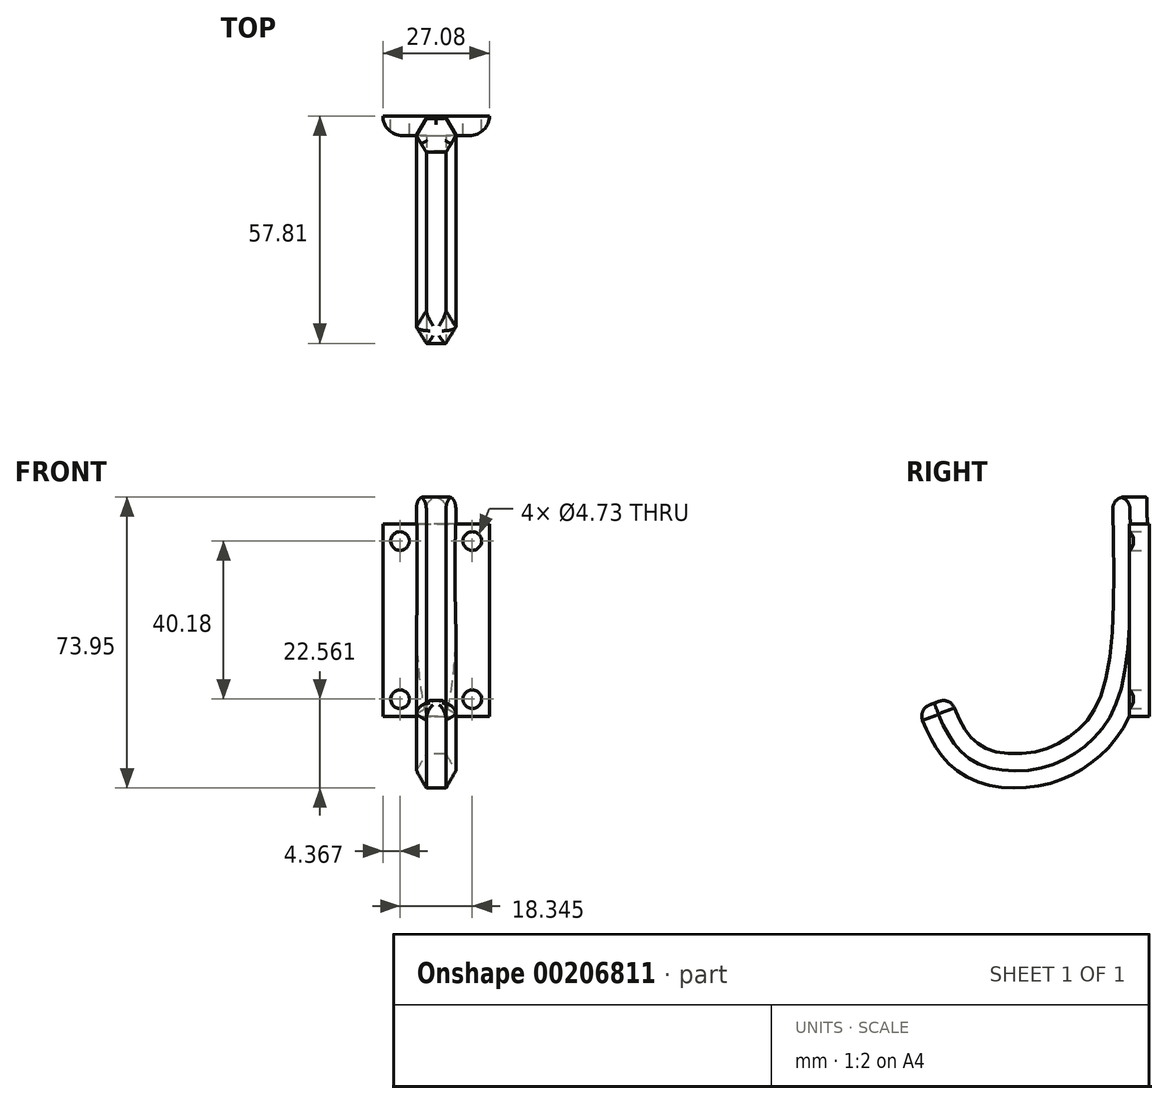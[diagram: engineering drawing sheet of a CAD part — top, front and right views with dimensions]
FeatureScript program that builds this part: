
annotation { "Feature Type Name" : "Feature", "Feature Type Description" : "" }
export const myFeature = defineFeature(function(context is Context, id is Id, definition is map)
    precondition{}
    {
        {
            var Q0;
            Q0=qCreatedBy(makeId("Right.planeOp"),FACE);
            var sketch = newSketch(context, id + "F0", { "sketchPlane" : qUnion([Q0])});
            skFitSpline(sketch, "E0", {"points": [v(0, 0) * mm, v(-2.5, -49.93) * mm, v(-11.35, -63.32) * mm, v(-22.92, -69) * mm, v(-37.22, -68.31) * mm, v(-44.94, -62.19) * mm, v(-49.7, -52.43) * mm], "startDerivative": vector(4.9, -203.53) * mm, "endDerivative": vector(-31.5, 78.26) * mm});
            skSolve(sketch);
        }
        {
            var Q0;
            Q0=qCreatedBy(makeId("Top.planeOp"),FACE);
            var sketch = newSketch(context, id + "F1", { "sketchPlane" : qUnion([Q0])});
            skCircle(sketch, "E1.cCircle", {"center": v(0, 0) * mm, "radius": 5 * mm, "construction": true});
            skLineSegment(sketch, "E1.0", {"start": v(5, 0) * mm, "end": v(2.5, -4.33) * mm});
            skLineSegment(sketch, "E1.1", {"start": v(2.5, -4.33) * mm, "end": v(-2.5, -4.33) * mm});
            skLineSegment(sketch, "E1.2", {"start": v(-2.5, -4.33) * mm, "end": v(-5, 0) * mm});
            skLineSegment(sketch, "E1.3", {"start": v(-5, 0) * mm, "end": v(-2.5, 4.33) * mm});
            skLineSegment(sketch, "E1.4", {"start": v(-2.5, 4.33) * mm, "end": v(2.5, 4.33) * mm});
            skLineSegment(sketch, "E1.5", {"start": v(2.5, 4.33) * mm, "end": v(5, 0) * mm});
            skSolve(sketch);
        }
        {
            var Q0;
            Q0=makeQuery(id+"F1.imprint","IMPRINT",FACE,{"disambiguationData":[TD([[makeQuery(id+"F1.imprint","IMPRINT",EDGE,{"derivedFrom":sQuery(id+"F1.wireOp",EDGE,"E1.0")}),-1.0]])]});
            var Q1;
            Q1=sQuery(id+"F0.wireOp",EDGE,"E0");
            sweep(context, id + "F2", {"profiles" : qUnion([Q0]), "path" : qUnion([Q1])});
        }
        {
            var Q0;
            Q0=makeQuery(id+"F2.opSweep","CAP_FACE",FACE,{"disambiguationData":[OSD([sQuery(id+"F0.wireOp",VERTEX,"E0.end"),sQuery(id+"F1.wireOp",EDGE,"E1.0"),sQuery(id+"F1.wireOp",EDGE,"E1.1"),sQuery(id+"F1.wireOp",EDGE,"E1.2"),sQuery(id+"F1.wireOp",EDGE,"E1.3"),sQuery(id+"F1.wireOp",EDGE,"E1.4"),sQuery(id+"F1.wireOp",EDGE,"E1.5")])],"isStart":false});
            var Q1;
            Q1=makeQuery(id+"F2.opSweep","CAP_EDGE",EDGE,{"disambiguationData":[OSD([sQuery(id+"F0.wireOp",VERTEX,"E0.start"),sQuery(id+"F1.wireOp",EDGE,"E1.1")])],"isStart":true});
            var Q2;
            Q2=makeQuery(id+"F2.opSweep","CAP_EDGE",EDGE,{"disambiguationData":[OSD([sQuery(id+"F0.wireOp",VERTEX,"E0.start"),sQuery(id+"F1.wireOp",EDGE,"E1.5")])],"isStart":true});
            var Q3;
            Q3=makeQuery(id+"F2.opSweep","CAP_EDGE",EDGE,{"disambiguationData":[OSD([sQuery(id+"F0.wireOp",VERTEX,"E0.start"),sQuery(id+"F1.wireOp",EDGE,"E1.3")])],"isStart":true});
            fillet(context, id + "F3", {"entities" : qUnion([Q0, Q1, Q2, Q3]), "radius" : 3 * mm, "tangentPropagation" : true, "allowEdgeOverflow" : false});
        }
        {
            var Q0;
            Q0=qCreatedBy(makeId("Front.planeOp"),FACE);
            var sketch = newSketch(context, id + "F4", { "sketchPlane" : qUnion([Q0])});
            skLineSegment(sketch, "E2.bottom", {"start": v(-13.54, -55.75) * mm, "end": v(13.54, -55.75) * mm});
            skLineSegment(sketch, "E2.top", {"start": v(-13.54, -6.84) * mm, "end": v(13.54, -6.84) * mm});
            skLineSegment(sketch, "E2.left", {"start": v(-13.54, -55.75) * mm, "end": v(-13.54, -6.84) * mm});
            skLineSegment(sketch, "E2.right", {"start": v(13.54, -55.75) * mm, "end": v(13.54, -6.84) * mm});
            skPoint(sketch, "E2.middle", {"position": v(0, -31.3) * mm});
            skSolve(sketch);
        }
        {
            var Q0;
            Q0=makeQuery(id+"F4.imprint","IMPRINT",FACE,{"disambiguationData":[TD([[makeQuery(id+"F4.imprint","IMPRINT",EDGE,{"derivedFrom":sQuery(id+"F4.wireOp",EDGE,"E2.bottom")}),1.0]])]});
            extrude(context, id + "F5", {"entities" : qUnion([Q0]), "operationType" : NewBodyOperationType.ADD, "oppositeDirection" : true, "depth" : 5 * mm});
        }
        {
            var Q0;
            Q0=makeQuery(id+"F5.opExtrude","CAP_FACE",FACE,{"disambiguationData":[OSD([sQuery(id+"F4.wireOp",EDGE,"E2.bottom"),sQuery(id+"F4.wireOp",EDGE,"E2.top"),sQuery(id+"F4.wireOp",EDGE,"E2.left"),sQuery(id+"F4.wireOp",EDGE,"E2.right")])],"isStart":false});
            var sketch = newSketch(context, id + "F6", { "sketchPlane" : qUnion([Q0])});
            skCircle(sketch, "E3", {"center": v(-8.96, -11.58) * mm, "radius": 2.59 * mm});
            skSolve(sketch);
        }
        {
            var Q0;
            Q0=qSketchRegion(id+"F6",true);
            extrude(context, id + "F7", {"entities" : qUnion([Q0]), "operationType" : NewBodyOperationType.ADD, "depth" : 25 * mm});
        }
        {
            var Q0;
            Q0=makeQuery(id+"F7.opExtrude","CAP_FACE",FACE,{"disambiguationData":[OSD([sQuery(id+"F6.wireOp",EDGE,"E3")])],"isStart":false});
            extrude(context, id + "F8", {"entities" : qUnion([Q0]), "operationType" : NewBodyOperationType.REMOVE, "oppositeDirection" : true, "depth" : 25 * mm});
        }
        {
            var Q0;
            Q0=makeQuery(id+"F8.boolean.opBoolean","MERGE",FACE,{"derivedFrom":[makeQuery(id+"F5.opExtrude","CAP_FACE",FACE,{"disambiguationData":[OSD([sQuery(id+"F4.wireOp",EDGE,"E2.bottom"),sQuery(id+"F4.wireOp",EDGE,"E2.top"),sQuery(id+"F4.wireOp",EDGE,"E2.left"),sQuery(id+"F4.wireOp",EDGE,"E2.right")])],"isStart":false}),makeQuery(id+"F8.opExtrude","CAP_FACE",FACE,{"disambiguationData":[OSD([sQuery(id+"F6.wireOp",EDGE,"E3")])],"isStart":false})]});
            var sketch = newSketch(context, id + "F9", { "sketchPlane" : qUnion([Q0])});
            skCircle(sketch, "E4", {"center": v(-9.17, -11.2) * mm, "radius": 2.36 * mm});
            skCircle(sketch, "E5.0.1.0", {"center": v(-9.17, -51.39) * mm, "radius": 2.36 * mm});
            skCircle(sketch, "E5.1.0.0", {"center": v(9.17, -11.2) * mm, "radius": 2.36 * mm});
            skCircle(sketch, "E5.1.1.0", {"center": v(9.17, -51.39) * mm, "radius": 2.36 * mm});
            skLineSegment(sketch, "E5.direction1", {"start": v(-9.17, -11.2) * mm, "end": v(9.17, -11.2) * mm, "construction": true});
            skLineSegment(sketch, "E5.direction2", {"start": v(-9.17, -11.2) * mm, "end": v(-9.17, -51.39) * mm, "construction": true});
            skSolve(sketch);
        }
        {
            var Q0;
            Q0=makeQuery(id+"F9.imprint","IMPRINT",FACE,{"disambiguationData":[TD([[makeQuery(id+"F9.imprint","IMPRINT",EDGE,{"derivedFrom":sQuery(id+"F9.wireOp",EDGE,"E4")}),1.0]])]});
            var Q1;
            Q1=makeQuery(id+"F9.imprint","IMPRINT",FACE,{"disambiguationData":[TD([[makeQuery(id+"F9.imprint","IMPRINT",EDGE,{"derivedFrom":sQuery(id+"F9.wireOp",EDGE,"E5.1.0.0")}),1.0]])]});
            var Q2;
            Q2=makeQuery(id+"F9.imprint","IMPRINT",FACE,{"disambiguationData":[TD([[makeQuery(id+"F9.imprint","IMPRINT",EDGE,{"derivedFrom":sQuery(id+"F9.wireOp",EDGE,"E5.1.1.0")}),1.0]])]});
            var Q3;
            Q3=makeQuery(id+"F9.imprint","IMPRINT",FACE,{"disambiguationData":[TD([[makeQuery(id+"F9.imprint","IMPRINT",EDGE,{"derivedFrom":sQuery(id+"F9.wireOp",EDGE,"E5.0.1.0")}),1.0]])]});
            extrude(context, id + "F10", {"entities" : qUnion([Q0, Q1, Q2, Q3]), "operationType" : NewBodyOperationType.REMOVE, "oppositeDirection" : true, "depth" : 25 * mm});
        }
        {
            var Q0;
            Q0=makeQuery(id+"F5.opExtrude","CAP_EDGE",EDGE,{"disambiguationData":[OSD([sQuery(id+"F4.wireOp",EDGE,"E2.left")])],"isStart":true});
            var Q1;
            Q1=makeQuery(id+"F5.opExtrude","CAP_EDGE",EDGE,{"disambiguationData":[OSD([sQuery(id+"F4.wireOp",EDGE,"E2.right")])],"isStart":true});
            fillet(context, id + "F11", {"entities" : qUnion([Q0, Q1]), "radius" : 5 * mm, "tangentPropagation" : true, "allowEdgeOverflow" : false});
        }
    });
